# Revit family: REVIT-CONQ-STORAGE
name_source: partatom
category: Mechanical Equipment
revit_build: Autodesk Revit 2017 (Build: 20190507_1515(x64)
units: mm (PartAtom-declared; Revit-internal decimal feet)

## family parameters
Always vertical = No
Cut with Voids When Loaded = No
OmniClass Number = 23.75.00.00
OmniClass Title = Climate Control (HVAC)
Part Type = Normal
Room Calculation Point = No
Round Connector Dimension = Use Radius
Shared = No
Work Plane-Based = No

## types (1)
- L 160A-TR
    Assembly Code = D3020100
    BuildingReturnDiameter = 2"
    BuildingReturnHeight = 46 1/2"
    BuildingReturnLength = 17 7/8"
    BuildingReturnRadius = 1"
    ColdInletHeight = 12"
    ColdWaterInletDiameter = 2"
    ColdWaterInletLength = 17 7/8"
    ColdWaterInletRadius = 1"
    Description = Conquest® Storage Tank
    DrainHeight = 12"
    DrainPipeDiameter = 1"
    DrainPipeRadius = 1/2"
    HotWaterCenterOffset = 0"
    HotWaterOutletDiameter = 2"
    HotWaterOutletLength = 81 3/4"
    HotWaterOutletRadius = 1"
    Manufacturer = PVI Industries, LLC
    Model = L 160A-TR
    Modeling Code = ABO090507TAS1507ABC0905
    Normal = 90.00°
    OmniClass Code = 23.65.35.11.11
    OmniClass Title = Storage Water Heater
    OpeningHeight = 24 1/2"
    OpeningLocation = 6 7/8"
    OpeningWidth = 14 1/4"
    Piping Material = Copper Pipe
    ReliefValveDiameter = 1"
    ReliefValveHeight = 61 3/4"
    ReliefValveRadius = 1/2"
    Storage Capacity = 130 CF
    Tank Casing = PVC
    TankDiameter = 33 3/4"
    TankHeight = 80 3/4"
    TankRadius = 16 7/8"
    URL = www.pvi.com
    Version = 1.0
    Weight = 550
    Weight Units = lbs.

## geometry (parser evidence)
native form markers: Blend x10, Sweep x2
no freeform markers — native parametric forms only
